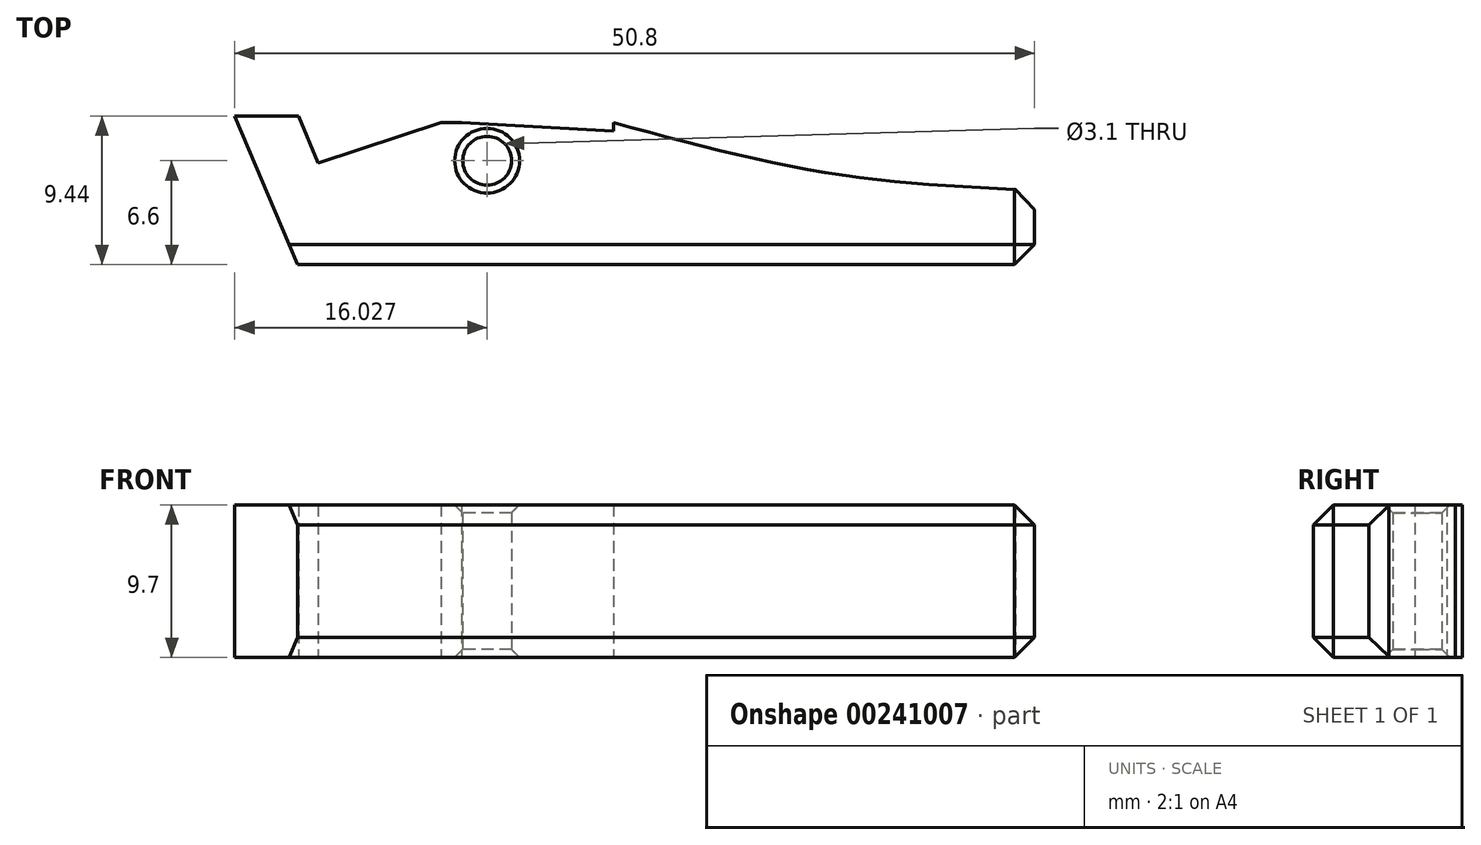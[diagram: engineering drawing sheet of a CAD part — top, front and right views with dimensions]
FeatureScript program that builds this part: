
annotation { "Feature Type Name" : "Feature", "Feature Type Description" : "" }
export const myFeature = defineFeature(function(context is Context, id is Id, definition is map)
    precondition{}
    {
        {
            var Q0;
            Q0=qCreatedBy(makeId("Top.planeOp"),FACE);
            var sketch = newSketch(context, id + "F0", { "sketchPlane" : qUnion([Q0])});
            skLineSegment(sketch, "E0.bottom", {"start": v(25.4, 4.72) * mm, "end": v(-11, 4.72) * mm});
            skLineSegment(sketch, "E0.top", {"start": v(25.4, -4.72) * mm, "end": v(-25.4, -4.72) * mm});
            skLineSegment(sketch, "E0.left", {"start": v(25.4, 4.72) * mm, "end": v(25.4, -4.72) * mm});
            skLineSegment(sketch, "E0.right", {"start": v(-25.4, 4.72) * mm, "end": v(-25.4, -4.72) * mm});
            skPoint(sketch, "E0.middle", {"position": v(0, 0) * mm});
            skLineSegment(sketch, "E1", {"start": v(-25.4, 4.72) * mm, "end": v(-21.4, -4.72) * mm});
            skLineSegment(sketch, "E2", {"start": v(-25.4, 4.72) * mm, "end": v(-21.36, 4.72) * mm});
            skLineSegment(sketch, "E3", {"start": v(-21.36, 4.72) * mm, "end": v(-20.1, 1.73) * mm});
            skLineSegment(sketch, "E4", {"start": v(-12.31, 4.3) * mm, "end": v(-20.1, 1.73) * mm});
            skLineSegment(sketch, "E5.trimOffspring", {"start": v(-21.36, 4.72) * mm, "end": v(-25.4, 4.72) * mm});
            skLineSegment(sketch, "E6.0", {"start": v(25.4, 4.3) * mm, "end": v(-11, 4.3) * mm});
            skLineSegment(sketch, "E7", {"start": v(-11, 4.3) * mm, "end": v(-12.31, 4.3) * mm});
            skLineSegment(sketch, "E8", {"start": v(-11, 4.3) * mm, "end": v(-1.35, 4.3) * mm});
            skLineSegment(sketch, "E9", {"start": v(-11, 4.3) * mm, "end": v(-1.35, 3.77) * mm});
            skLineSegment(sketch, "E10", {"start": v(-1.35, 3.77) * mm, "end": v(-1.35, 4.3) * mm});
            skFitSpline(sketch, "E11", {"points": [v(-1.35, 4.3) * mm, v(12.46, 1.08) * mm, v(25.4, 0) * mm], "startDerivative": vector(27.17, -7.33) * mm, "endDerivative": vector(26.32, -1.21) * mm});
            skCircle(sketch, "E12", {"center": v(-9.37, 1.88) * mm, "radius": 1.55 * mm});
            skSolve(sketch);
        }
        {
            var Q0;
            {var subQ0=sQuery(id+"F0.wireOp",EDGE,"E1");Q0=makeQuery(id+"F0.imprint","IMPRINT",FACE,{"disambiguationData":[TD([[makeQuery(id+"F0.imprint","IMPRINT",EDGE,{"derivedFrom":subQ0}),1.0]])]});}
            extrude(context, id + "F1", {"entities" : qUnion([Q0]), "depth" : 9.7 * mm});
        }
        {
            var Q0;
            Q0=makeQuery(id+"F1.opExtrude","SWEPT_FACE",FACE,{"disambiguationData":[OSD([sQuery(id+"F0.wireOp",EDGE,"E0.left")])]});
            var Q1;
            Q1=makeQuery(id+"F1.opExtrude","CAP_EDGE",EDGE,{"disambiguationData":[OSD([sQuery(id+"F0.wireOp",EDGE,"E0.top")])],"isStart":false});
            var Q2;
            Q2=makeQuery(id+"F1.opExtrude","CAP_EDGE",EDGE,{"disambiguationData":[OSD([sQuery(id+"F0.wireOp",EDGE,"E0.top")])],"isStart":true});
            chamfer(context, id + "F2", {"entities" : qUnion([Q0, Q1, Q2]), "width" : 1.27 * mm, "tangentPropagation" : true});
        }
        {
            var Q0;
            Q0=makeQuery(id+"F1.opExtrude","SWEPT_FACE",FACE,{"disambiguationData":[OSD([sQuery(id+"F0.wireOp",EDGE,"E12")])]});
            chamfer(context, id + "F3", {"entities" : qUnion([Q0]), "width" : 0.5 * mm, "tangentPropagation" : true});
        }
    });
